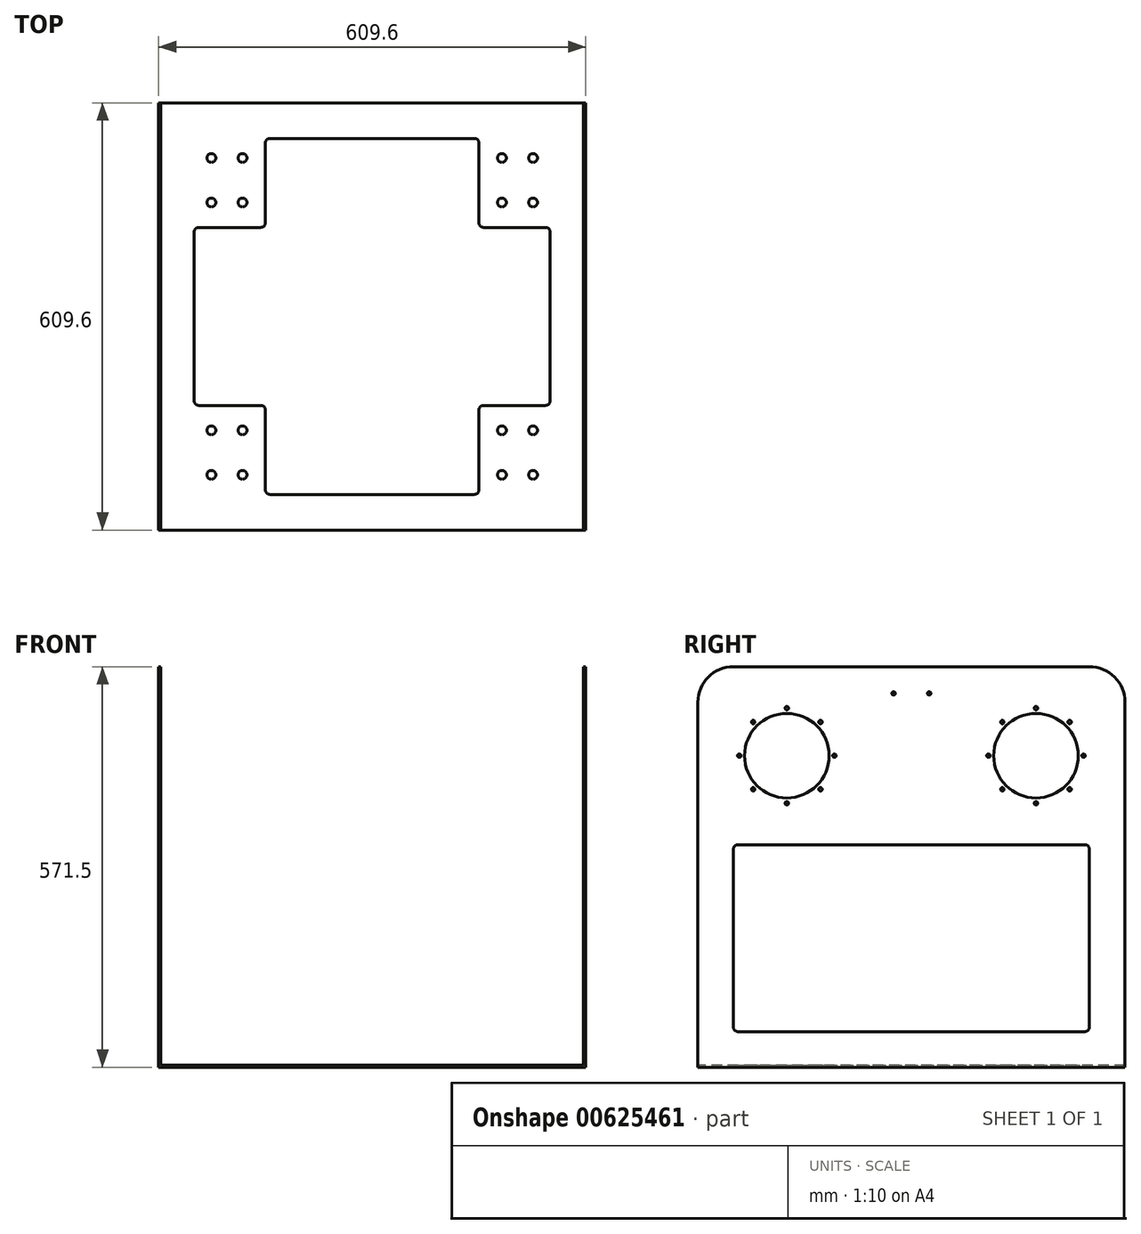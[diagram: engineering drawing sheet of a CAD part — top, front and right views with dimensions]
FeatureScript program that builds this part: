
annotation { "Feature Type Name" : "Feature", "Feature Type Description" : "" }
export const myFeature = defineFeature(function(context is Context, id is Id, definition is map)
    precondition{}
    {
        {
            var Q0;
            Q0=qCreatedBy(makeId("Top.planeOp"),FACE);
            var sketch = newSketch(context, id + "F0", { "sketchPlane" : qUnion([Q0])});
            skLineSegment(sketch, "E0.bottom", {"start": v(304.8, -304.8) * mm, "end": v(-304.8, -304.8) * mm});
            skLineSegment(sketch, "E0.top", {"start": v(304.8, 304.8) * mm, "end": v(-304.8, 304.8) * mm});
            skLineSegment(sketch, "E0.left", {"start": v(304.8, -304.8) * mm, "end": v(304.8, 304.8) * mm});
            skLineSegment(sketch, "E0.right", {"start": v(-304.8, -304.8) * mm, "end": v(-304.8, 304.8) * mm});
            skPoint(sketch, "E0.middle", {"position": v(0, 0) * mm});
            skSolve(sketch);
        }
        {
            var Q0;
            Q0 = qSketchRegion(id + "F0", true);
            extrude(context, id + "F1", {"entities" : qUnion([Q0]), "depth" : 571.5 * mm, "offsetDistance" : 25.4 * mm});
        }
        {
            var Q0;
            Q0=makeQuery(id+"F1.opExtrude","SWEPT_FACE",FACE,{"disambiguationData":[OSD([sQuery(id+"F0.wireOp",EDGE,"E0.bottom")])]});
            var sketch = newSketch(context, id + "F2", { "sketchPlane" : qUnion([Q0])});
            skLineSegment(sketch, "E1.bottom", {"start": v(-301.63, 571.5) * mm, "end": v(301.62, 571.5) * mm});
            skLineSegment(sketch, "E1.top", {"start": v(-301.63, 3.17) * mm, "end": v(301.62, 3.17) * mm});
            skLineSegment(sketch, "E1.left", {"start": v(-301.63, 571.5) * mm, "end": v(-301.63, 3.18) * mm});
            skLineSegment(sketch, "E1.right", {"start": v(301.62, 571.5) * mm, "end": v(301.62, 3.18) * mm});
            skSolve(sketch);
        }
        {
            var Q0;
            Q0 = qSketchRegion(id + "F2", true);
            extrude(context, id + "F3", {"entities" : qUnion([Q0]), "operationType" : NewBodyOperationType.REMOVE, "endBound" : BoundingType.THROUGH_ALL, "oppositeDirection" : true, "depth" : 25.4 * mm, "offsetDistance" : 25.4 * mm});
        }
        {
            var Q0;
            Q0=makeQuery(id+"F1.opExtrude","SWEPT_FACE",FACE,{"disambiguationData":[OSD([sQuery(id+"F0.wireOp",EDGE,"E0.left")])]});
            var sketch = newSketch(context, id + "F4", { "sketchPlane" : qUnion([Q0])});
            skArc(sketch, "E2", {"start": v(-254, 571.5) * mm, "mid": v(-289.92, 556.62) * mm, "end": v(-304.8, 520.7) * mm});
            skArc(sketch, "E3", {"start": v(304.8, 520.7) * mm, "mid": v(289.92, 556.62) * mm, "end": v(254, 571.5) * mm});
            skLineSegment(sketch, "E4", {"start": v(-304.8, 571.5) * mm, "end": v(-304.8, 520.7) * mm});
            skLineSegment(sketch, "E5", {"start": v(-304.8, 571.5) * mm, "end": v(-254, 571.5) * mm});
            skLineSegment(sketch, "E6", {"start": v(254, 571.5) * mm, "end": v(304.8, 571.5) * mm});
            skLineSegment(sketch, "E7", {"start": v(304.8, 571.5) * mm, "end": v(304.8, 520.7) * mm});
            skSolve(sketch);
        }
        {
            var Q0;
            Q0=makeQuery(id+"F4.imprint","IMPRINT",FACE,{"disambiguationData":[TD([[makeQuery(id+"F4.imprint","IMPRINT",EDGE,{"derivedFrom":sQuery(id+"F4.wireOp",EDGE,"E3")}),-1.0]])]});
            var Q1;
            Q1=makeQuery(id+"F4.imprint","IMPRINT",FACE,{"disambiguationData":[TD([[makeQuery(id+"F4.imprint","IMPRINT",EDGE,{"derivedFrom":sQuery(id+"F4.wireOp",EDGE,"E2")}),-1.0]])]});
            extrude(context, id + "F5", {"entities" : qUnion([Q0, Q1]), "operationType" : NewBodyOperationType.REMOVE, "endBound" : BoundingType.THROUGH_ALL, "oppositeDirection" : true, "depth" : 25.4 * mm, "offsetDistance" : 25.4 * mm});
        }
        {
            var Q0;
            Q0=makeQuery(id+"F1.opExtrude","SWEPT_FACE",FACE,{"disambiguationData":[OSD([sQuery(id+"F0.wireOp",EDGE,"E0.left")])]});
            var sketch = newSketch(context, id + "F6", { "sketchPlane" : qUnion([Q0])});
            skLineSegment(sketch, "E8", {"start": v(-304.8, 520.7) * mm, "end": v(-304.8, 0) * mm});
            skLineSegment(sketch, "E9", {"start": v(-304.8, 0) * mm, "end": v(304.8, 0) * mm});
            skLineSegment(sketch, "E10", {"start": v(304.8, 0) * mm, "end": v(304.8, 520.7) * mm});
            skLineSegment(sketch, "E11", {"start": v(-254, 571.5) * mm, "end": v(254, 571.5) * mm});
            skLineSegment(sketch, "E12.0", {"start": v(254, 57.15) * mm, "end": v(254, 311.15) * mm});
            skLineSegment(sketch, "E12.1", {"start": v(-247.65, 50.8) * mm, "end": v(247.65, 50.8) * mm});
            skLineSegment(sketch, "E12.2", {"start": v(-254, 311.15) * mm, "end": v(-254, 57.15) * mm});
            skLineSegment(sketch, "E13.0", {"start": v(-247.65, 317.5) * mm, "end": v(247.65, 317.5) * mm});
            skPoint(sketch, "E14.visualSharp", {"position": v(-254, 317.5) * mm});
            skArc(sketch, "E14.filletArc", {"start": v(-247.65, 317.5) * mm, "mid": v(-252.14, 315.64) * mm, "end": v(-254, 311.15) * mm});
            skPoint(sketch, "E15.visualSharp", {"position": v(254, 317.5) * mm});
            skArc(sketch, "E15.filletArc", {"start": v(254, 311.15) * mm, "mid": v(252.14, 315.64) * mm, "end": v(247.65, 317.5) * mm});
            skPoint(sketch, "E16.visualSharp", {"position": v(254, 50.8) * mm});
            skArc(sketch, "E16.filletArc", {"start": v(247.65, 50.8) * mm, "mid": v(252.14, 52.66) * mm, "end": v(254, 57.15) * mm});
            skPoint(sketch, "E17.visualSharp", {"position": v(-254, 50.8) * mm});
            skArc(sketch, "E17.filletArc", {"start": v(-254, 57.15) * mm, "mid": v(-252.14, 52.66) * mm, "end": v(-247.65, 50.8) * mm});
            skSolve(sketch);
        }
        {
            var Q0;
            Q0 = qSketchRegion(id + "F6", true);
            extrude(context, id + "F7", {"entities" : qUnion([Q0]), "operationType" : NewBodyOperationType.REMOVE, "endBound" : BoundingType.THROUGH_ALL, "oppositeDirection" : true, "depth" : 25.4 * mm, "offsetDistance" : 25.4 * mm});
        }
        {
            var Q0;
            Q0=makeQuery(id+"F1.opExtrude","SWEPT_FACE",FACE,{"disambiguationData":[OSD([sQuery(id+"F0.wireOp",EDGE,"E0.left")])]});
            var sketch = newSketch(context, id + "F8", { "sketchPlane" : qUnion([Q0])});
            skCircle(sketch, "E18", {"center": v(-177.8, 444.5) * mm, "radius": 60.33 * mm});
            skLineSegment(sketch, "E19", {"start": v(-177.8, 504.82) * mm, "end": v(-177.8, 509.9) * mm});
            skCircle(sketch, "E20", {"center": v(-177.8, 512.38) * mm, "radius": 2.48 * mm});
            skLineSegment(sketch, "E21", {"start": v(-177.8, 512.38) * mm, "end": v(-177.8, 509.9) * mm});
            skLineSegment(sketch, "E22", {"start": v(-177.8, 444.5) * mm, "end": v(-112.4, 444.5) * mm});
            skLineSegment(sketch, "E23", {"start": v(-177.8, 444.5) * mm, "end": v(-177.8, 379.1) * mm});
            skLineSegment(sketch, "E24", {"start": v(-177.8, 444.5) * mm, "end": v(-243.2, 444.5) * mm});
            skCircle(sketch, "E25", {"center": v(-245.68, 444.5) * mm, "radius": 2.48 * mm});
            skCircle(sketch, "E26", {"center": v(-109.92, 444.5) * mm, "radius": 2.48 * mm});
            skLineSegment(sketch, "E27", {"start": v(-245.68, 444.5) * mm, "end": v(-243.2, 444.5) * mm});
            skLineSegment(sketch, "E28", {"start": v(-109.92, 444.5) * mm, "end": v(-112.4, 444.5) * mm});
            skCircle(sketch, "E29", {"center": v(-177.8, 376.62) * mm, "radius": 2.48 * mm});
            skLineSegment(sketch, "E30", {"start": v(-177.8, 376.62) * mm, "end": v(-177.8, 379.1) * mm});
            skLineSegment(sketch, "E31", {"start": v(-177.8, 444.5) * mm, "end": v(-129.8, 492.5) * mm});
            skLineSegment(sketch, "E32", {"start": v(-177.8, 444.5) * mm, "end": v(-129.8, 396.5) * mm});
            skLineSegment(sketch, "E33", {"start": v(-177.8, 444.5) * mm, "end": v(-225.8, 396.5) * mm});
            skLineSegment(sketch, "E34", {"start": v(-177.8, 444.5) * mm, "end": v(-225.8, 492.5) * mm});
            skCircle(sketch, "E35", {"center": v(-129.8, 396.5) * mm, "radius": 2.48 * mm});
            skCircle(sketch, "E36", {"center": v(-129.8, 492.5) * mm, "radius": 2.48 * mm});
            skCircle(sketch, "E37", {"center": v(-225.8, 396.5) * mm, "radius": 2.48 * mm});
            skCircle(sketch, "E38", {"center": v(-225.8, 492.5) * mm, "radius": 2.48 * mm});
            skLineSegment(sketch, "E39", {"start": v(0, 571.5) * mm, "end": v(0, 317.5) * mm});
            skLineSegment(sketch, "E40.MirrorCS", {"start": v(177.8, 376.62) * mm, "end": v(177.8, 379.1) * mm});
            skCircle(sketch, "E41.MirrorC", {"center": v(177.8, 376.62) * mm, "radius": 2.48 * mm});
            skCircle(sketch, "E42.MirrorC", {"center": v(129.8, 492.5) * mm, "radius": 2.48 * mm});
            skCircle(sketch, "E43.MirrorC", {"center": v(225.8, 396.5) * mm, "radius": 2.48 * mm});
            skCircle(sketch, "E44.MirrorC", {"center": v(225.8, 492.5) * mm, "radius": 2.48 * mm});
            skCircle(sketch, "E45.MirrorC", {"center": v(177.8, 512.38) * mm, "radius": 2.48 * mm});
            skLineSegment(sketch, "E46.MirrorCS", {"start": v(177.8, 512.38) * mm, "end": v(177.8, 509.9) * mm});
            skLineSegment(sketch, "E47.MirrorCS", {"start": v(109.92, 444.5) * mm, "end": v(112.4, 444.5) * mm});
            skCircle(sketch, "E48.MirrorC", {"center": v(129.8, 396.5) * mm, "radius": 2.48 * mm});
            skLineSegment(sketch, "E49.MirrorCS", {"start": v(177.8, 504.83) * mm, "end": v(177.8, 509.9) * mm});
            skLineSegment(sketch, "E50.MirrorCS", {"start": v(245.68, 444.5) * mm, "end": v(243.2, 444.5) * mm});
            skCircle(sketch, "E51.MirrorC", {"center": v(109.92, 444.5) * mm, "radius": 2.48 * mm});
            skCircle(sketch, "E52.MirrorC", {"center": v(245.68, 444.5) * mm, "radius": 2.48 * mm});
            skLineSegment(sketch, "E53.MirrorCS", {"start": v(177.8, 444.5) * mm, "end": v(225.8, 492.5) * mm});
            skLineSegment(sketch, "E54.MirrorCS", {"start": v(177.8, 444.5) * mm, "end": v(129.8, 396.5) * mm});
            skLineSegment(sketch, "E55.MirrorCS", {"start": v(177.8, 444.5) * mm, "end": v(129.8, 492.5) * mm});
            skLineSegment(sketch, "E56.MirrorCS", {"start": v(177.8, 444.5) * mm, "end": v(225.8, 396.5) * mm});
            skLineSegment(sketch, "E57.MirrorCS", {"start": v(177.8, 444.5) * mm, "end": v(112.4, 444.5) * mm});
            skCircle(sketch, "E58.MirrorC", {"center": v(177.8, 444.5) * mm, "radius": 60.33 * mm});
            skLineSegment(sketch, "E59.MirrorCS", {"start": v(177.8, 444.5) * mm, "end": v(177.8, 379.1) * mm});
            skLineSegment(sketch, "E60.MirrorCS", {"start": v(177.8, 444.5) * mm, "end": v(243.2, 444.5) * mm});
            skSolve(sketch);
        }
        {
            var Q0;
            Q0 = qSketchRegion(id + "F8", true);
            extrude(context, id + "F9", {"entities" : qUnion([Q0]), "operationType" : NewBodyOperationType.REMOVE, "endBound" : BoundingType.THROUGH_ALL, "oppositeDirection" : true, "depth" : 25.4 * mm, "offsetDistance" : 25.4 * mm});
        }
        {
            var Q0;
            Q0=makeQuery(id+"F1.opExtrude","CAP_FACE",FACE,{"disambiguationData":[OSD([sQuery(id+"F0.wireOp",EDGE,"E0.bottom"),sQuery(id+"F0.wireOp",EDGE,"E0.top"),sQuery(id+"F0.wireOp",EDGE,"E0.left"),sQuery(id+"F0.wireOp",EDGE,"E0.right")])],"isStart":true});
            var sketch = newSketch(context, id + "F10", { "sketchPlane" : qUnion([Q0])});
            skLineSegment(sketch, "E61", {"start": v(-146.05, 254) * mm, "end": v(146.05, 254) * mm});
            skLineSegment(sketch, "E62", {"start": v(-152.4, 247.65) * mm, "end": v(-152.4, 133.35) * mm});
            skLineSegment(sketch, "E63", {"start": v(152.4, 247.65) * mm, "end": v(152.4, 133.35) * mm});
            skLineSegment(sketch, "E64", {"start": v(158.75, 127) * mm, "end": v(247.65, 127) * mm});
            skLineSegment(sketch, "E65", {"start": v(-158.75, 127) * mm, "end": v(-247.65, 127) * mm});
            skLineSegment(sketch, "E66", {"start": v(-254, 120.65) * mm, "end": v(-254, -120.65) * mm});
            skLineSegment(sketch, "E67", {"start": v(-247.65, -127) * mm, "end": v(-158.75, -127) * mm});
            skLineSegment(sketch, "E68", {"start": v(-152.4, -133.35) * mm, "end": v(-152.4, -247.65) * mm});
            skLineSegment(sketch, "E69", {"start": v(-146.05, -254) * mm, "end": v(146.05, -254) * mm});
            skLineSegment(sketch, "E70", {"start": v(152.4, -247.65) * mm, "end": v(152.4, -133.35) * mm});
            skLineSegment(sketch, "E71", {"start": v(158.75, -127) * mm, "end": v(247.65, -127) * mm});
            skLineSegment(sketch, "E72", {"start": v(254, -120.65) * mm, "end": v(254, 120.65) * mm});
            skPoint(sketch, "E73.visualSharp", {"position": v(-152.4, 254) * mm});
            skArc(sketch, "E73.filletArc", {"start": v(-146.05, 254) * mm, "mid": v(-150.54, 252.14) * mm, "end": v(-152.4, 247.65) * mm});
            skPoint(sketch, "E74.visualSharp", {"position": v(152.4, 254) * mm});
            skArc(sketch, "E74.filletArc", {"start": v(152.4, 247.65) * mm, "mid": v(150.54, 252.14) * mm, "end": v(146.05, 254) * mm});
            skPoint(sketch, "E75.visualSharp", {"position": v(152.4, 127) * mm});
            skArc(sketch, "E75.filletArc", {"start": v(152.4, 133.35) * mm, "mid": v(154.26, 128.86) * mm, "end": v(158.75, 127) * mm});
            skPoint(sketch, "E76.visualSharp", {"position": v(254, 127) * mm});
            skArc(sketch, "E76.filletArc", {"start": v(254, 120.65) * mm, "mid": v(252.14, 125.14) * mm, "end": v(247.65, 127) * mm});
            skPoint(sketch, "E77.visualSharp", {"position": v(254, -127) * mm});
            skArc(sketch, "E77.filletArc", {"start": v(247.65, -127) * mm, "mid": v(252.14, -125.14) * mm, "end": v(254, -120.65) * mm});
            skPoint(sketch, "E78.visualSharp", {"position": v(152.4, -127) * mm});
            skArc(sketch, "E78.filletArc", {"start": v(158.75, -127) * mm, "mid": v(154.26, -128.86) * mm, "end": v(152.4, -133.35) * mm});
            skPoint(sketch, "E79.visualSharp", {"position": v(152.4, -254) * mm});
            skArc(sketch, "E79.filletArc", {"start": v(146.05, -254) * mm, "mid": v(150.54, -252.14) * mm, "end": v(152.4, -247.65) * mm});
            skPoint(sketch, "E80.visualSharp", {"position": v(-152.4, -254) * mm});
            skArc(sketch, "E80.filletArc", {"start": v(-152.4, -247.65) * mm, "mid": v(-150.54, -252.14) * mm, "end": v(-146.05, -254) * mm});
            skPoint(sketch, "E81.visualSharp", {"position": v(-152.4, -127) * mm});
            skArc(sketch, "E81.filletArc", {"start": v(-152.4, -133.35) * mm, "mid": v(-154.26, -128.86) * mm, "end": v(-158.75, -127) * mm});
            skPoint(sketch, "E82.visualSharp", {"position": v(-254, -127) * mm});
            skArc(sketch, "E82.filletArc", {"start": v(-254, -120.65) * mm, "mid": v(-252.14, -125.14) * mm, "end": v(-247.65, -127) * mm});
            skPoint(sketch, "E83.visualSharp", {"position": v(-254, 127) * mm});
            skArc(sketch, "E83.filletArc", {"start": v(-247.65, 127) * mm, "mid": v(-252.14, 125.14) * mm, "end": v(-254, 120.65) * mm});
            skPoint(sketch, "E84.visualSharp", {"position": v(-152.4, 127) * mm});
            skArc(sketch, "E84.filletArc", {"start": v(-158.75, 127) * mm, "mid": v(-154.26, 128.86) * mm, "end": v(-152.4, 133.35) * mm});
            skLineSegment(sketch, "E85", {"start": v(-152.4, 190.5) * mm, "end": v(-304.8, 190.5) * mm});
            skLineSegment(sketch, "E86", {"start": v(152.4, 190.5) * mm, "end": v(304.8, 190.5) * mm});
            skLineSegment(sketch, "E87", {"start": v(0, 254) * mm, "end": v(0, 304.8) * mm});
            skLineSegment(sketch, "E88", {"start": v(0, -254) * mm, "end": v(0, -304.8) * mm});
            skSolve(sketch);
        }
        {
            var Q0;
            Q0 = qSketchRegion(id + "F10", true);
            extrude(context, id + "F11", {"entities" : qUnion([Q0]), "operationType" : NewBodyOperationType.REMOVE, "endBound" : BoundingType.THROUGH_ALL, "oppositeDirection" : true, "depth" : 25.4 * mm, "offsetDistance" : 25.4 * mm});
        }
        {
            var Q0;
            Q0=makeQuery(id+"F1.opExtrude","CAP_FACE",FACE,{"disambiguationData":[OSD([sQuery(id+"F0.wireOp",EDGE,"E0.bottom"),sQuery(id+"F0.wireOp",EDGE,"E0.top"),sQuery(id+"F0.wireOp",EDGE,"E0.left"),sQuery(id+"F0.wireOp",EDGE,"E0.right")])],"isStart":true});
            var sketch = newSketch(context, id + "F12", { "sketchPlane" : qUnion([Q0])});
            skCircle(sketch, "E89", {"center": v(-229.54, 226.06) * mm, "radius": 6.35 * mm});
            skCircle(sketch, "E90", {"center": v(-185.09, 226.06) * mm, "radius": 6.35 * mm});
            skCircle(sketch, "E91", {"center": v(-229.54, 162.56) * mm, "radius": 6.35 * mm});
            skCircle(sketch, "E92", {"center": v(-185.09, 162.56) * mm, "radius": 6.35 * mm});
            skLineSegment(sketch, "E93", {"start": v(0, 254) * mm, "end": v(0, -254) * mm});
            skLineSegment(sketch, "E94", {"start": v(-254, 0) * mm, "end": v(254, 0) * mm});
            skCircle(sketch, "E95.MirrorC", {"center": v(185.09, 226.06) * mm, "radius": 6.35 * mm});
            skCircle(sketch, "E96.MirrorC", {"center": v(229.54, 226.06) * mm, "radius": 6.35 * mm});
            skCircle(sketch, "E97.MirrorC", {"center": v(229.54, 162.56) * mm, "radius": 6.35 * mm});
            skCircle(sketch, "E98.MirrorC", {"center": v(185.09, 162.56) * mm, "radius": 6.35 * mm});
            skCircle(sketch, "E99.MirrorC", {"center": v(229.54, -162.56) * mm, "radius": 6.35 * mm});
            skCircle(sketch, "E100.MirrorC", {"center": v(229.54, -226.06) * mm, "radius": 6.35 * mm});
            skCircle(sketch, "E101.MirrorC", {"center": v(185.09, -226.06) * mm, "radius": 6.35 * mm});
            skCircle(sketch, "E102.MirrorC", {"center": v(185.09, -162.56) * mm, "radius": 6.35 * mm});
            skCircle(sketch, "E103.MirrorC", {"center": v(-185.09, -226.06) * mm, "radius": 6.35 * mm});
            skCircle(sketch, "E104.MirrorC", {"center": v(-185.09, -162.56) * mm, "radius": 6.35 * mm});
            skCircle(sketch, "E105.MirrorC", {"center": v(-229.54, -162.56) * mm, "radius": 6.35 * mm});
            skCircle(sketch, "E106.MirrorC", {"center": v(-229.54, -226.06) * mm, "radius": 6.35 * mm});
            skSolve(sketch);
        }
        {
            var Q0;
            Q0 = qSketchRegion(id + "F12", true);
            extrude(context, id + "F13", {"entities" : qUnion([Q0]), "operationType" : NewBodyOperationType.REMOVE, "endBound" : BoundingType.THROUGH_ALL, "oppositeDirection" : true, "depth" : 25.4 * mm, "offsetDistance" : 25.4 * mm});
        }
        {
            var Q0;
            Q0=makeQuery(id+"F1.opExtrude","SWEPT_FACE",FACE,{"disambiguationData":[OSD([sQuery(id+"F0.wireOp",EDGE,"E0.left")])]});
            var sketch = newSketch(context, id + "F14", { "sketchPlane" : qUnion([Q0])});
            skCircle(sketch, "E107", {"center": v(-25.4, 533.4) * mm, "radius": 2.48 * mm});
            skCircle(sketch, "E108", {"center": v(25.4, 533.4) * mm, "radius": 2.48 * mm});
            skLineSegment(sketch, "E109", {"start": v(-25.4, 533.4) * mm, "end": v(-303.19, 533.4) * mm});
            skLineSegment(sketch, "E110", {"start": v(25.4, 533.4) * mm, "end": v(303.19, 533.4) * mm});
            skSolve(sketch);
        }
        {
            var Q0;
            Q0 = qSketchRegion(id + "F14", true);
            extrude(context, id + "F15", {"entities" : qUnion([Q0]), "operationType" : NewBodyOperationType.REMOVE, "endBound" : BoundingType.THROUGH_ALL, "oppositeDirection" : true, "depth" : 25.4 * mm, "offsetDistance" : 25.4 * mm});
        }
    });
